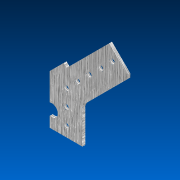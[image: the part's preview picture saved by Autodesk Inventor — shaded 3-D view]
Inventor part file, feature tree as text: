
AUTODESK INVENTOR PART (.ipt)
format: ipt  version: 2022.2 (Build 262287000, 287)  size: 145,408 bytes
history: native  units: in
note: dims shown in document units (in); Inventor stores cm internally (conversion verified against a paired STEP export)
features: other x4, reference x2, extrude x1, sketch x1, fillet x1
ambient origin geometry x8: Origin, YZ Plane, XZ Plane, XY Plane, X Axis, Y Axis, Z Axis, Center Point
bodies: Solid1 (feature_tree)
feature tree (9):
  extrude  "Extrusion1"  Depth=1.85in
  sketch  "Sketch1"  dims[d0=0.125in d1=1.85in d2=0.375in d3=0.0in d4=0.0in]
  reference  "Reference1"
  reference  "Reference3"
  fillet  "Fillet2"  Radius=0.375in
  parser-record x1  (decoder bookkeeping rows leaked as tree rows — omitted from the tree; the rows remain in map.json)
  other  "Chassis.iam"
  other  "#8-32 x 2.500 Star Drive Screw (276-8016):6"
  other  "1 x 2 x 0.100 x 39 Inside Chassis Pre-Drilled VersaFrame Aluminum Tube Stock Cut (217-3453):1"
note: 1 file-system path scrubbed to <path> (originals preserved in map.json)
